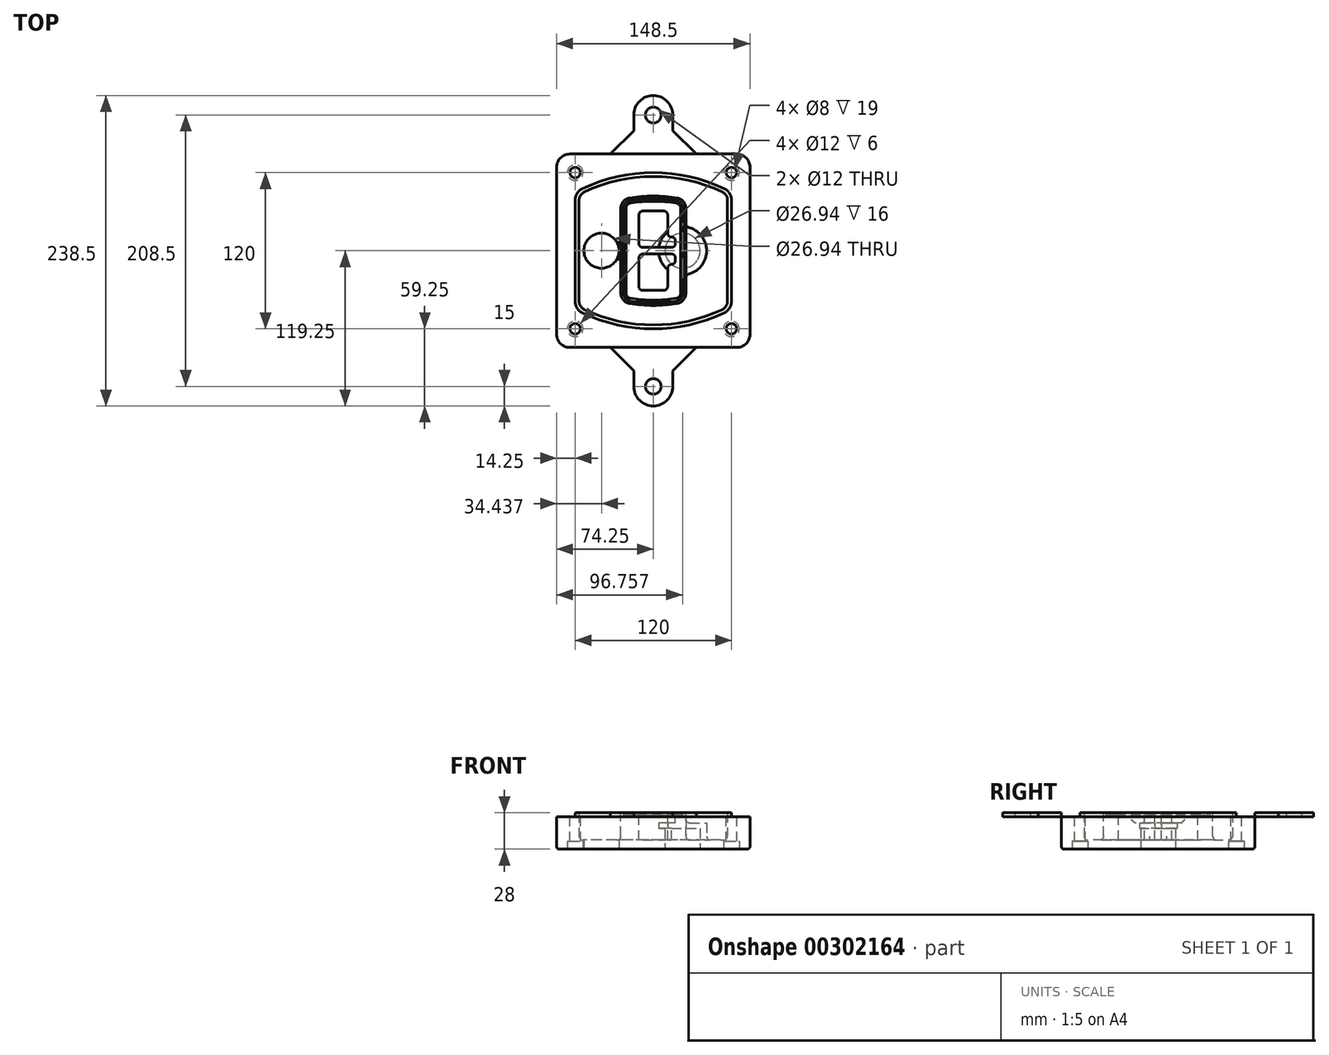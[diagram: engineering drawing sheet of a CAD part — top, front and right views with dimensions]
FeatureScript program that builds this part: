
annotation { "Feature Type Name" : "Feature", "Feature Type Description" : "" }
export const myFeature = defineFeature(function(context is Context, id is Id, definition is map)
    precondition{}
    {
        {
            var Q0;
            Q0=qCreatedBy(makeId("Top.planeOp"),FACE);
            var sketch = newSketch(context, id + "F0", { "sketchPlane" : qUnion([Q0])});
            skPoint(sketch, "E0.rect.middle", {"position": v(0, 0) * mm});
            skLineSegment(sketch, "E1.bottom", {"start": v(-64.25, -74.25) * mm, "end": v(64.25, -74.25) * mm});
            skLineSegment(sketch, "E1.top", {"start": v(-64.25, 74.25) * mm, "end": v(64.25, 74.25) * mm});
            skLineSegment(sketch, "E1.left", {"start": v(-74.25, -64.25) * mm, "end": v(-74.25, 64.25) * mm});
            skLineSegment(sketch, "E1.right", {"start": v(74.25, -64.25) * mm, "end": v(74.25, 64.25) * mm});
            skLineSegment(sketch, "E2", {"start": v(-74.25, 74.25) * mm, "end": v(74.25, -74.25) * mm, "construction": true});
            skLineSegment(sketch, "E3", {"start": v(74.25, 74.25) * mm, "end": v(-74.25, -74.25) * mm, "construction": true});
            skCircle(sketch, "E4", {"center": v(-60, 60) * mm, "radius": 4 * mm});
            skCircle(sketch, "E5", {"center": v(60, 60) * mm, "radius": 4 * mm});
            skCircle(sketch, "E6", {"center": v(60, -60) * mm, "radius": 4 * mm});
            skCircle(sketch, "E7", {"center": v(-60, -60) * mm, "radius": 4 * mm});
            skLineSegment(sketch, "E8", {"start": v(-60, 60) * mm, "end": v(60, 60) * mm, "construction": true});
            skLineSegment(sketch, "E9", {"start": v(60, 60) * mm, "end": v(60, -60) * mm, "construction": true});
            skLineSegment(sketch, "E10", {"start": v(60, -60) * mm, "end": v(-60, -60) * mm, "construction": true});
            skLineSegment(sketch, "E11", {"start": v(-60, -60) * mm, "end": v(-60, 60) * mm, "construction": true});
            skLineSegment(sketch, "E12", {"start": v(-60, 38.83) * mm, "end": v(-60, -38.83) * mm});
            skLineSegment(sketch, "E13", {"start": v(60, 38.83) * mm, "end": v(60, -38.83) * mm});
            skArc(sketch, "E14", {"start": v(54.26, 47.88) * mm, "mid": v(0, 60) * mm, "end": v(-54.26, 47.88) * mm});
            skArc(sketch, "E15", {"start": v(-54.26, -47.88) * mm, "mid": v(0, -60) * mm, "end": v(54.26, -47.88) * mm});
            skLineSegment(sketch, "E16", {"start": v(-60, 0) * mm, "end": v(60, 0) * mm, "construction": true});
            skPoint(sketch, "E17.visualSharp", {"position": v(-60, -45) * mm});
            skArc(sketch, "E17.filletArc", {"start": v(-60, -38.83) * mm, "mid": v(-58.44, -44.2) * mm, "end": v(-54.26, -47.88) * mm});
            skPoint(sketch, "E18.visualSharp", {"position": v(-60, 45) * mm});
            skArc(sketch, "E18.filletArc", {"start": v(-54.26, 47.88) * mm, "mid": v(-58.44, 44.2) * mm, "end": v(-60, 38.83) * mm});
            skPoint(sketch, "E19.visualSharp", {"position": v(60, 45) * mm});
            skArc(sketch, "E19.filletArc", {"start": v(60, 38.83) * mm, "mid": v(58.44, 44.2) * mm, "end": v(54.26, 47.88) * mm});
            skPoint(sketch, "E20.visualSharp", {"position": v(60, -45) * mm});
            skArc(sketch, "E20.filletArc", {"start": v(54.26, -47.88) * mm, "mid": v(58.44, -44.2) * mm, "end": v(60, -38.83) * mm});
            skPoint(sketch, "E21.visualSharp", {"position": v(-74.25, 74.25) * mm});
            skArc(sketch, "E21.filletArc", {"start": v(-64.25, 74.25) * mm, "mid": v(-71.32, 71.32) * mm, "end": v(-74.25, 64.25) * mm});
            skPoint(sketch, "E22.visualSharp", {"position": v(74.25, 74.25) * mm});
            skArc(sketch, "E22.filletArc", {"start": v(74.25, 64.25) * mm, "mid": v(71.32, 71.32) * mm, "end": v(64.25, 74.25) * mm});
            skPoint(sketch, "E23.visualSharp", {"position": v(74.25, -74.25) * mm});
            skArc(sketch, "E23.filletArc", {"start": v(64.25, -74.25) * mm, "mid": v(71.32, -71.32) * mm, "end": v(74.25, -64.25) * mm});
            skPoint(sketch, "E24.visualSharp", {"position": v(-74.25, -74.25) * mm});
            skArc(sketch, "E24.filletArc", {"start": v(-74.25, -64.25) * mm, "mid": v(-71.32, -71.32) * mm, "end": v(-64.25, -74.25) * mm});
            skArc(sketch, "E25.0", {"start": v(57, 38.83) * mm, "mid": v(55.9, 42.58) * mm, "end": v(52.98, 45.17) * mm});
            skLineSegment(sketch, "E25.1", {"start": v(57, 38.83) * mm, "end": v(57, -38.83) * mm});
            skArc(sketch, "E25.2", {"start": v(52.98, -45.17) * mm, "mid": v(55.9, -42.58) * mm, "end": v(57, -38.83) * mm});
            skArc(sketch, "E25.3", {"start": v(-52.98, -45.17) * mm, "mid": v(0, -57) * mm, "end": v(52.98, -45.17) * mm});
            skArc(sketch, "E25.4", {"start": v(-57, -38.83) * mm, "mid": v(-55.9, -42.58) * mm, "end": v(-52.98, -45.17) * mm});
            skArc(sketch, "E25.5", {"start": v(52.98, 45.17) * mm, "mid": v(0, 57) * mm, "end": v(-52.98, 45.17) * mm});
            skLineSegment(sketch, "E25.6", {"start": v(-57, 38.83) * mm, "end": v(-57, -38.83) * mm});
            skArc(sketch, "E25.7", {"start": v(-52.98, 45.17) * mm, "mid": v(-55.9, 42.58) * mm, "end": v(-57, 38.83) * mm});
            skArc(sketch, "E26.0", {"start": v(-55.96, 51.5) * mm, "mid": v(-61.82, 46.33) * mm, "end": v(-64, 38.83) * mm});
            skArc(sketch, "E26.1", {"start": v(55.96, 51.5) * mm, "mid": v(0, 64) * mm, "end": v(-55.96, 51.5) * mm});
            skArc(sketch, "E26.2", {"start": v(64, 38.83) * mm, "mid": v(61.82, 46.33) * mm, "end": v(55.96, 51.5) * mm});
            skLineSegment(sketch, "E26.3", {"start": v(64, 38.83) * mm, "end": v(64, -38.83) * mm});
            skArc(sketch, "E26.4", {"start": v(55.96, -51.5) * mm, "mid": v(61.82, -46.33) * mm, "end": v(64, -38.83) * mm});
            skLineSegment(sketch, "E26.5", {"start": v(-64, 38.83) * mm, "end": v(-64, -38.83) * mm});
            skArc(sketch, "E26.6", {"start": v(-55.96, -51.5) * mm, "mid": v(0, -64) * mm, "end": v(55.96, -51.5) * mm});
            skArc(sketch, "E26.7", {"start": v(-64, -38.83) * mm, "mid": v(-61.82, -46.33) * mm, "end": v(-55.96, -51.5) * mm});
            skSolve(sketch);
        }
        {
            var Q0;
            Q0=makeQuery(id+"F0.imprint","IMPRINT",FACE,{"disambiguationData":[TD([[makeQuery(id+"F0.imprint","IMPRINT",EDGE,{"derivedFrom":sQuery(id+"F0.wireOp",EDGE,"E1.bottom")}),1.0]])]});
            var Q1;
            Q1=makeQuery(id+"F0.imprint","IMPRINT",FACE,{"disambiguationData":[TD([[makeQuery(id+"F0.imprint","IMPRINT",EDGE,{"derivedFrom":sQuery(id+"F0.wireOp",EDGE,"E12")}),1.0]])]});
            var Q2;
            Q2=makeQuery(id+"F0.imprint","IMPRINT",FACE,{"disambiguationData":[TD([[makeQuery(id+"F0.imprint","IMPRINT",EDGE,{"derivedFrom":sQuery(id+"F0.wireOp",EDGE,"E25.0")}),1.0]])]});
            var Q3;
            Q3=makeQuery(id+"F0.imprint","IMPRINT",FACE,{"disambiguationData":[TD([[makeQuery(id+"F0.imprint","IMPRINT",EDGE,{"derivedFrom":sQuery(id+"F0.wireOp",EDGE,"E12")}),-1.0]])]});
            extrude(context, id + "F1", {"entities" : qUnion([Q0, Q1, Q2, Q3]), "oppositeDirection" : true, "depth" : 25 * mm});
        }
        {
            var Q0;
            Q0=makeQuery(id+"F0.imprint","IMPRINT",FACE,{"disambiguationData":[TD([[makeQuery(id+"F0.imprint","IMPRINT",EDGE,{"derivedFrom":sQuery(id+"F0.wireOp",EDGE,"E12")}),1.0]])]});
            extrude(context, id + "F2", {"entities" : qUnion([Q0]), "operationType" : NewBodyOperationType.ADD, "depth" : 3 * mm});
        }
        {
            var Q0;
            Q0=makeQuery(id+"F0.imprint","IMPRINT",FACE,{"disambiguationData":[TD([[makeQuery(id+"F0.imprint","IMPRINT",EDGE,{"derivedFrom":sQuery(id+"F0.wireOp",EDGE,"E25.0")}),1.0]])]});
            extrude(context, id + "F3", {"entities" : qUnion([Q0]), "operationType" : NewBodyOperationType.REMOVE, "oppositeDirection" : true, "depth" : 18 * mm});
        }
        {
            var Q0;
            Q0=makeQuery(id+"F2.opExtrude","CAP_FACE",FACE,{"disambiguationData":[OSD([sQuery(id+"F0.wireOp",EDGE,"E12"),sQuery(id+"F0.wireOp",EDGE,"E13"),sQuery(id+"F0.wireOp",EDGE,"E14"),sQuery(id+"F0.wireOp",EDGE,"E15"),sQuery(id+"F0.wireOp",EDGE,"E17.filletArc"),sQuery(id+"F0.wireOp",EDGE,"E18.filletArc"),sQuery(id+"F0.wireOp",EDGE,"E19.filletArc"),sQuery(id+"F0.wireOp",EDGE,"E20.filletArc"),sQuery(id+"F0.wireOp",EDGE,"E25.0"),sQuery(id+"F0.wireOp",EDGE,"E25.1"),sQuery(id+"F0.wireOp",EDGE,"E25.2"),sQuery(id+"F0.wireOp",EDGE,"E25.3"),sQuery(id+"F0.wireOp",EDGE,"E25.4"),sQuery(id+"F0.wireOp",EDGE,"E25.5"),sQuery(id+"F0.wireOp",EDGE,"E25.6"),sQuery(id+"F0.wireOp",EDGE,"E25.7")])],"isStart":false});
            var sketch = newSketch(context, id + "F4", { "sketchPlane" : qUnion([Q0])});
            skArc(sketch, "E27.0", {"start": v(-18.34, -40.45) * mm, "mid": v(0, -42) * mm, "end": v(18.34, -40.45) * mm});
            skArc(sketch, "E28.0", {"start": v(18.34, 40.45) * mm, "mid": v(0, 42) * mm, "end": v(-18.34, 40.45) * mm});
            skLineSegment(sketch, "E29", {"start": v(-25, 32.57) * mm, "end": v(-25, -32.57) * mm});
            skLineSegment(sketch, "E30", {"start": v(25, 32.57) * mm, "end": v(25, -32.57) * mm});
            skLineSegment(sketch, "E31", {"start": v(-25, 39.1) * mm, "end": v(25, 39.1) * mm, "construction": true});
            skLineSegment(sketch, "E32", {"start": v(-25, -39.1) * mm, "end": v(25, -39.1) * mm, "construction": true});
            skPoint(sketch, "E33.visualSharp", {"position": v(-25, 39.1) * mm});
            skArc(sketch, "E33.filletArc", {"start": v(-18.34, 40.45) * mm, "mid": v(-23.11, 37.73) * mm, "end": v(-25, 32.57) * mm});
            skPoint(sketch, "E34.visualSharp", {"position": v(25, 39.1) * mm});
            skArc(sketch, "E34.filletArc", {"start": v(25, 32.57) * mm, "mid": v(23.11, 37.73) * mm, "end": v(18.34, 40.45) * mm});
            skPoint(sketch, "E35.visualSharp", {"position": v(25, -39.1) * mm});
            skArc(sketch, "E35.filletArc", {"start": v(18.34, -40.45) * mm, "mid": v(23.11, -37.73) * mm, "end": v(25, -32.57) * mm});
            skPoint(sketch, "E36.visualSharp", {"position": v(-25, -39.1) * mm});
            skArc(sketch, "E36.filletArc", {"start": v(-25, -32.57) * mm, "mid": v(-23.11, -37.73) * mm, "end": v(-18.34, -40.45) * mm});
            skArc(sketch, "E37.0", {"start": v(52.98, 45.17) * mm, "mid": v(0, 57) * mm, "end": v(-52.98, 45.17) * mm});
            skArc(sketch, "E37.1", {"start": v(-52.98, 45.17) * mm, "mid": v(-55.9, 42.58) * mm, "end": v(-57, 38.83) * mm});
            skLineSegment(sketch, "E37.2", {"start": v(-57, 38.83) * mm, "end": v(-57, -38.83) * mm});
            skArc(sketch, "E37.3", {"start": v(-57, -38.83) * mm, "mid": v(-55.9, -42.58) * mm, "end": v(-52.98, -45.17) * mm});
            skArc(sketch, "E37.4", {"start": v(-52.98, -45.17) * mm, "mid": v(0, -57) * mm, "end": v(52.98, -45.17) * mm});
            skArc(sketch, "E37.5", {"start": v(52.98, -45.17) * mm, "mid": v(55.9, -42.58) * mm, "end": v(57, -38.83) * mm});
            skLineSegment(sketch, "E37.6", {"start": v(57, 38.83) * mm, "end": v(57, -38.83) * mm});
            skArc(sketch, "E37.7", {"start": v(57, 38.83) * mm, "mid": v(55.9, 42.58) * mm, "end": v(52.98, 45.17) * mm});
            skLineSegment(sketch, "E38.0", {"start": v(23, 32.57) * mm, "end": v(23, -32.57) * mm});
            skArc(sketch, "E38.1", {"start": v(18, -38.48) * mm, "mid": v(21.58, -36.44) * mm, "end": v(23, -32.57) * mm});
            skArc(sketch, "E38.2", {"start": v(-18, -38.48) * mm, "mid": v(0, -40) * mm, "end": v(18, -38.48) * mm});
            skArc(sketch, "E38.3", {"start": v(-23, -32.57) * mm, "mid": v(-21.58, -36.44) * mm, "end": v(-18, -38.48) * mm});
            skLineSegment(sketch, "E38.4", {"start": v(-23, 32.57) * mm, "end": v(-23, -32.57) * mm});
            skArc(sketch, "E38.5", {"start": v(23, 32.57) * mm, "mid": v(21.58, 36.44) * mm, "end": v(18, 38.48) * mm});
            skArc(sketch, "E38.6", {"start": v(-18, 38.48) * mm, "mid": v(-21.58, 36.44) * mm, "end": v(-23, 32.57) * mm});
            skArc(sketch, "E38.7", {"start": v(18, 38.48) * mm, "mid": v(0, 40) * mm, "end": v(-18, 38.48) * mm});
            skArc(sketch, "E39.0", {"start": v(21, 32.57) * mm, "mid": v(20.06, 35.15) * mm, "end": v(17.67, 36.5) * mm});
            skLineSegment(sketch, "E39.1", {"start": v(21, 32.57) * mm, "end": v(21, -32.57) * mm});
            skArc(sketch, "E39.2", {"start": v(17.67, -36.5) * mm, "mid": v(20.06, -35.15) * mm, "end": v(21, -32.57) * mm});
            skArc(sketch, "E39.3", {"start": v(-17.67, -36.5) * mm, "mid": v(0, -38) * mm, "end": v(17.67, -36.5) * mm});
            skArc(sketch, "E39.4", {"start": v(-21, -32.57) * mm, "mid": v(-20.06, -35.15) * mm, "end": v(-17.67, -36.5) * mm});
            skArc(sketch, "E39.5", {"start": v(17.67, 36.5) * mm, "mid": v(0, 38) * mm, "end": v(-17.67, 36.5) * mm});
            skLineSegment(sketch, "E39.6", {"start": v(-21, 32.57) * mm, "end": v(-21, -32.57) * mm});
            skArc(sketch, "E39.7", {"start": v(-17.67, 36.5) * mm, "mid": v(-20.06, 35.15) * mm, "end": v(-21, 32.57) * mm});
            skLineSegment(sketch, "E40", {"start": v(-25, 0) * mm, "end": v(25, 0) * mm, "construction": true});
            skLineSegment(sketch, "E41", {"start": v(-11, 5.5) * mm, "end": v(-11, 27.5) * mm});
            skLineSegment(sketch, "E42", {"start": v(-8, 30.5) * mm, "end": v(8, 30.5) * mm});
            skLineSegment(sketch, "E43", {"start": v(11, 27.5) * mm, "end": v(11, 13.5) * mm});
            skLineSegment(sketch, "E44", {"start": v(14, 10.5) * mm, "end": v(14, 10.5) * mm});
            skLineSegment(sketch, "E45", {"start": v(17, 7.5) * mm, "end": v(17, 5.5) * mm});
            skLineSegment(sketch, "E46", {"start": v(14, 2.5) * mm, "end": v(-8, 2.5) * mm});
            skPoint(sketch, "E47.visualSharp", {"position": v(-11, 30.5) * mm});
            skArc(sketch, "E47.filletArc", {"start": v(-8, 30.5) * mm, "mid": v(-10.12, 29.62) * mm, "end": v(-11, 27.5) * mm});
            skPoint(sketch, "E48.visualSharp", {"position": v(11, 30.5) * mm});
            skArc(sketch, "E48.filletArc", {"start": v(11, 27.5) * mm, "mid": v(10.12, 29.62) * mm, "end": v(8, 30.5) * mm});
            skPoint(sketch, "E49.visualSharp", {"position": v(11, 10.5) * mm});
            skArc(sketch, "E49.filletArc", {"start": v(11, 13.5) * mm, "mid": v(11.88, 11.38) * mm, "end": v(14, 10.5) * mm});
            skPoint(sketch, "E50.visualSharp", {"position": v(17, 10.5) * mm});
            skArc(sketch, "E50.filletArc", {"start": v(17, 7.5) * mm, "mid": v(16.12, 9.62) * mm, "end": v(14, 10.5) * mm});
            skPoint(sketch, "E51.visualSharp", {"position": v(17, 2.5) * mm});
            skArc(sketch, "E51.filletArc", {"start": v(14, 2.5) * mm, "mid": v(16.12, 3.38) * mm, "end": v(17, 5.5) * mm});
            skPoint(sketch, "E52.visualSharp", {"position": v(-11, 2.5) * mm});
            skArc(sketch, "E52.filletArc", {"start": v(-11, 5.5) * mm, "mid": v(-10.12, 3.38) * mm, "end": v(-8, 2.5) * mm});
            skLineSegment(sketch, "E53.0.MirrorCS", {"start": v(14, -2.5) * mm, "end": v(-8, -2.5) * mm});
            skArc(sketch, "E54.0.MirrorCS", {"start": v(-11, -5.5) * mm, "mid": v(-10.12, -3.38) * mm, "end": v(-8, -2.5) * mm});
            skLineSegment(sketch, "E55.0.MirrorCS", {"start": v(-11, -5.5) * mm, "end": v(-11, -27.5) * mm});
            skArc(sketch, "E56.0.MirrorCS", {"start": v(-8, -30.5) * mm, "mid": v(-10.12, -29.62) * mm, "end": v(-11, -27.5) * mm});
            skLineSegment(sketch, "E57.0.MirrorCS", {"start": v(-8, -30.5) * mm, "end": v(8, -30.5) * mm});
            skArc(sketch, "E58.0.MirrorCS", {"start": v(11, -27.5) * mm, "mid": v(10.12, -29.62) * mm, "end": v(8, -30.5) * mm});
            skLineSegment(sketch, "E59.0.MirrorCS", {"start": v(11, -27.5) * mm, "end": v(11, -13.5) * mm});
            skArc(sketch, "E60.0.MirrorCS", {"start": v(11, -13.5) * mm, "mid": v(11.88, -11.38) * mm, "end": v(14, -10.5) * mm});
            skArc(sketch, "E61.0.MirrorCS", {"start": v(17, -7.5) * mm, "mid": v(16.12, -9.62) * mm, "end": v(14, -10.5) * mm});
            skLineSegment(sketch, "E62.0.MirrorCS", {"start": v(17, -7.5) * mm, "end": v(17, -5.5) * mm});
            skArc(sketch, "E63.0.MirrorCS", {"start": v(14, -2.5) * mm, "mid": v(16.12, -3.38) * mm, "end": v(17, -5.5) * mm});
            skSolve(sketch);
        }
        {
            var Q0;
            Q0=makeQuery(id+"F4.imprint","IMPRINT",FACE,{"disambiguationData":[TD([[makeQuery(id+"F4.imprint","IMPRINT",EDGE,{"derivedFrom":sQuery(id+"F4.wireOp",EDGE,"E27.0")}),1.0]])]});
            var Q1;
            Q1=makeQuery(id+"F4.imprint","IMPRINT",FACE,{"disambiguationData":[TD([[makeQuery(id+"F4.imprint","IMPRINT",EDGE,{"derivedFrom":sQuery(id+"F4.wireOp",EDGE,"E38.0")}),-1.0]])]});
            var Q2;
            Q2=makeQuery(id+"F4.imprint","IMPRINT",FACE,{"disambiguationData":[TD([[makeQuery(id+"F4.imprint","IMPRINT",EDGE,{"derivedFrom":sQuery(id+"F4.wireOp",EDGE,"E39.0")}),1.0]])]});
            extrude(context, id + "F5", {"entities" : qUnion([Q0, Q1, Q2]), "operationType" : NewBodyOperationType.ADD, "endBound" : BoundingType.UP_TO_NEXT, "oppositeDirection" : true, "depth" : 25 * mm});
        }
        {
            var Q0;
            Q0=makeQuery(id+"F4.imprint","IMPRINT",FACE,{"disambiguationData":[TD([[makeQuery(id+"F4.imprint","IMPRINT",EDGE,{"derivedFrom":sQuery(id+"F4.wireOp",EDGE,"E38.0")}),-1.0]])]});
            extrude(context, id + "F6", {"entities" : qUnion([Q0]), "operationType" : NewBodyOperationType.REMOVE, "oppositeDirection" : true, "depth" : 2 * mm});
        }
        {
            var Q0;
            Q0=makeQuery(id+"F1.opExtrude","CAP_FACE",FACE,{"disambiguationData":[OSD([sQuery(id+"F0.wireOp",EDGE,"E1.bottom"),sQuery(id+"F0.wireOp",EDGE,"E1.top"),sQuery(id+"F0.wireOp",EDGE,"E1.left"),sQuery(id+"F0.wireOp",EDGE,"E1.right"),sQuery(id+"F0.wireOp",EDGE,"E4"),sQuery(id+"F0.wireOp",EDGE,"E5"),sQuery(id+"F0.wireOp",EDGE,"E6"),sQuery(id+"F0.wireOp",EDGE,"E7"),sQuery(id+"F0.wireOp",EDGE,"E21.filletArc"),sQuery(id+"F0.wireOp",EDGE,"E22.filletArc"),sQuery(id+"F0.wireOp",EDGE,"E23.filletArc"),sQuery(id+"F0.wireOp",EDGE,"E24.filletArc")])],"isStart":false});
            var sketch = newSketch(context, id + "F7", { "sketchPlane" : qUnion([Q0])});
            skCircle(sketch, "E64", {"center": v(22.5, 0) * mm, "radius": 13.47 * mm});
            skCircle(sketch, "E65", {"center": v(-39.81, 0) * mm, "radius": 13.47 * mm});
            skLineSegment(sketch, "E66", {"start": v(74.25, 0) * mm, "end": v(-74.25, 0) * mm});
            skCircle(sketch, "E67", {"center": v(22.5, 0) * mm, "radius": 18.47 * mm});
            skCircle(sketch, "E68", {"center": v(60, -60) * mm, "radius": 6 * mm});
            skCircle(sketch, "E69", {"center": v(-60, -60) * mm, "radius": 6 * mm});
            skCircle(sketch, "E70", {"center": v(-60, 60) * mm, "radius": 6 * mm});
            skCircle(sketch, "E71", {"center": v(60, 60) * mm, "radius": 6 * mm});
            skSolve(sketch);
        }
        {
            var Q0;
            {var subQ1=sQuery(id+"F7.wireOp",EDGE,"E66");var subQ4=sQuery(id+"F7.wireOp",EDGE,"E64");var subQ6=makeQuery(id+"F7.imprint","INTERSECT",VERTEX,{"disambiguationData":[OD(0.0)],"derivedFrom":[subQ4,subQ1]});Q0=makeQuery(id+"F7.imprint","IMPRINT",FACE,{"disambiguationData":[TD([[makeQuery(id+"F7.imprint","IMPRINT",EDGE,{"disambiguationData":[TD([[subQ6,-1.0]])],"derivedFrom":subQ4}),-1.0]])]});}
            var Q1;
            {var subQ0=sQuery(id+"F7.wireOp",EDGE,"E66");var subQ1=sQuery(id+"F7.wireOp",EDGE,"E64");var subQ3=makeQuery(id+"F7.imprint","INTERSECT",VERTEX,{"disambiguationData":[OD(0.0)],"derivedFrom":[subQ1,subQ0]});Q1=makeQuery(id+"F7.imprint","IMPRINT",FACE,{"disambiguationData":[TD([[makeQuery(id+"F7.imprint","IMPRINT",EDGE,{"disambiguationData":[TD([[subQ3,-1.0]])],"derivedFrom":subQ1}),1.0]])]});}
            var Q2;
            {var subQ0=sQuery(id+"F7.wireOp",EDGE,"E66");var subQ1=sQuery(id+"F7.wireOp",EDGE,"E64");var subQ3=makeQuery(id+"F7.imprint","INTERSECT",VERTEX,{"disambiguationData":[OD(0.0)],"derivedFrom":[subQ1,subQ0]});Q2=makeQuery(id+"F7.imprint","IMPRINT",FACE,{"disambiguationData":[TD([[makeQuery(id+"F7.imprint","IMPRINT",EDGE,{"disambiguationData":[TD([[subQ3,1.0]])],"derivedFrom":subQ1}),1.0]])]});}
            var Q3;
            {var subQ1=sQuery(id+"F7.wireOp",EDGE,"E66");var subQ4=sQuery(id+"F7.wireOp",EDGE,"E64");var subQ6=makeQuery(id+"F7.imprint","INTERSECT",VERTEX,{"disambiguationData":[OD(0.0)],"derivedFrom":[subQ4,subQ1]});Q3=makeQuery(id+"F7.imprint","IMPRINT",FACE,{"disambiguationData":[TD([[makeQuery(id+"F7.imprint","IMPRINT",EDGE,{"disambiguationData":[TD([[subQ6,1.0]])],"derivedFrom":subQ4}),-1.0]])]});}
            extrude(context, id + "F8", {"entities" : qUnion([Q0, Q1, Q2, Q3]), "operationType" : NewBodyOperationType.ADD, "oppositeDirection" : true, "depth" : 20 * mm});
        }
        {
            var Q0;
            {var subQ0=sQuery(id+"F7.wireOp",EDGE,"E66");var subQ1=sQuery(id+"F7.wireOp",EDGE,"E64");var subQ3=makeQuery(id+"F7.imprint","INTERSECT",VERTEX,{"disambiguationData":[OD(0.0)],"derivedFrom":[subQ1,subQ0]});Q0=makeQuery(id+"F7.imprint","IMPRINT",FACE,{"disambiguationData":[TD([[makeQuery(id+"F7.imprint","IMPRINT",EDGE,{"disambiguationData":[TD([[subQ3,-1.0]])],"derivedFrom":subQ1}),1.0]])]});}
            var Q1;
            {var subQ0=sQuery(id+"F7.wireOp",EDGE,"E66");var subQ1=sQuery(id+"F7.wireOp",EDGE,"E64");var subQ3=makeQuery(id+"F7.imprint","INTERSECT",VERTEX,{"disambiguationData":[OD(0.0)],"derivedFrom":[subQ1,subQ0]});Q1=makeQuery(id+"F7.imprint","IMPRINT",FACE,{"disambiguationData":[TD([[makeQuery(id+"F7.imprint","IMPRINT",EDGE,{"disambiguationData":[TD([[subQ3,1.0]])],"derivedFrom":subQ1}),1.0]])]});}
            extrude(context, id + "F9", {"entities" : qUnion([Q0, Q1]), "operationType" : NewBodyOperationType.REMOVE, "oppositeDirection" : true, "depth" : 16 * mm});
        }
        {
            var Q0;
            {var subQ0=sQuery(id+"F7.wireOp",EDGE,"E66");var subQ1=sQuery(id+"F7.wireOp",EDGE,"E65");var subQ3=makeQuery(id+"F7.imprint","INTERSECT",VERTEX,{"disambiguationData":[OD(0.0)],"derivedFrom":[subQ1,subQ0]});Q0=makeQuery(id+"F7.imprint","IMPRINT",FACE,{"disambiguationData":[TD([[makeQuery(id+"F7.imprint","IMPRINT",EDGE,{"disambiguationData":[TD([[subQ3,-1.0]])],"derivedFrom":subQ1}),1.0]])]});}
            var Q1;
            {var subQ0=sQuery(id+"F7.wireOp",EDGE,"E66");var subQ1=sQuery(id+"F7.wireOp",EDGE,"E65");var subQ3=makeQuery(id+"F7.imprint","INTERSECT",VERTEX,{"disambiguationData":[OD(0.0)],"derivedFrom":[subQ1,subQ0]});Q1=makeQuery(id+"F7.imprint","IMPRINT",FACE,{"disambiguationData":[TD([[makeQuery(id+"F7.imprint","IMPRINT",EDGE,{"disambiguationData":[TD([[subQ3,1.0]])],"derivedFrom":subQ1}),1.0]])]});}
            extrude(context, id + "F10", {"entities" : qUnion([Q0, Q1]), "operationType" : NewBodyOperationType.REMOVE, "oppositeDirection" : true, "depth" : 25 * mm});
        }
        {
            var Q0;
            Q0=makeQuery(id+"F7.imprint","IMPRINT",FACE,{"disambiguationData":[TD([[makeQuery(id+"F7.imprint","IMPRINT",EDGE,{"derivedFrom":sQuery(id+"F7.wireOp",EDGE,"E68")}),1.0]])]});
            var Q1;
            Q1=makeQuery(id+"F7.imprint","IMPRINT",FACE,{"disambiguationData":[TD([[makeQuery(id+"F7.imprint","IMPRINT",EDGE,{"derivedFrom":makeQuery(id+"F1.opExtrude","CAP_EDGE",EDGE,{"disambiguationData":[OSD([sQuery(id+"F0.wireOp",EDGE,"E5")])],"isStart":false})}),-1.0]])]});
            var Q2;
            Q2=makeQuery(id+"F7.imprint","IMPRINT",FACE,{"disambiguationData":[TD([[makeQuery(id+"F7.imprint","IMPRINT",EDGE,{"derivedFrom":sQuery(id+"F7.wireOp",EDGE,"E69")}),1.0]])]});
            var Q3;
            Q3=makeQuery(id+"F7.imprint","IMPRINT",FACE,{"disambiguationData":[TD([[makeQuery(id+"F7.imprint","IMPRINT",EDGE,{"derivedFrom":makeQuery(id+"F1.opExtrude","CAP_EDGE",EDGE,{"disambiguationData":[OSD([sQuery(id+"F0.wireOp",EDGE,"E4")])],"isStart":false})}),-1.0]])]});
            var Q4;
            Q4=makeQuery(id+"F7.imprint","IMPRINT",FACE,{"disambiguationData":[TD([[makeQuery(id+"F7.imprint","IMPRINT",EDGE,{"derivedFrom":sQuery(id+"F7.wireOp",EDGE,"E70")}),1.0]])]});
            var Q5;
            Q5=makeQuery(id+"F7.imprint","IMPRINT",FACE,{"disambiguationData":[TD([[makeQuery(id+"F7.imprint","IMPRINT",EDGE,{"derivedFrom":makeQuery(id+"F1.opExtrude","CAP_EDGE",EDGE,{"disambiguationData":[OSD([sQuery(id+"F0.wireOp",EDGE,"E7")])],"isStart":false})}),-1.0]])]});
            var Q6;
            Q6=makeQuery(id+"F7.imprint","IMPRINT",FACE,{"disambiguationData":[TD([[makeQuery(id+"F7.imprint","IMPRINT",EDGE,{"derivedFrom":sQuery(id+"F7.wireOp",EDGE,"E71")}),1.0]])]});
            var Q7;
            Q7=makeQuery(id+"F7.imprint","IMPRINT",FACE,{"disambiguationData":[TD([[makeQuery(id+"F7.imprint","IMPRINT",EDGE,{"derivedFrom":makeQuery(id+"F1.opExtrude","CAP_EDGE",EDGE,{"disambiguationData":[OSD([sQuery(id+"F0.wireOp",EDGE,"E6")])],"isStart":false})}),-1.0]])]});
            extrude(context, id + "F11", {"entities" : qUnion([Q0, Q1, Q2, Q3, Q4, Q5, Q6, Q7]), "operationType" : NewBodyOperationType.REMOVE, "oppositeDirection" : true, "depth" : 6 * mm});
        }
        {
            var Q0;
            Q0=makeQuery(id+"F9.boolean.opBoolean","COPY",FACE,{"derivedFrom":makeQuery(id+"F9.opExtrude","CAP_FACE",FACE,{"disambiguationData":[OSD([sQuery(id+"F7.wireOp",EDGE,"E64")])],"isStart":false})});
            var sketch = newSketch(context, id + "F12", { "sketchPlane" : qUnion([Q0])});
            skArc(sketch, "E72.0", {"start": v(11, 14.45) * mm, "mid": v(6.45, 9.13) * mm, "end": v(4.2, 2.5) * mm});
            skArc(sketch, "E72.1", {"start": v(4.2, -2.5) * mm, "mid": v(6.45, -9.13) * mm, "end": v(11, -14.45) * mm});
            skLineSegment(sketch, "E73", {"start": v(4.2, -2.5) * mm, "end": v(14, -2.5) * mm});
            skLineSegment(sketch, "E74.0", {"start": v(14, 2.5) * mm, "end": v(4.2, 2.5) * mm});
            skArc(sketch, "E74.1", {"start": v(14, 2.5) * mm, "mid": v(16.12, 3.38) * mm, "end": v(17, 5.5) * mm});
            skLineSegment(sketch, "E74.2", {"start": v(17, 7.5) * mm, "end": v(17, 5.5) * mm});
            skArc(sketch, "E74.3", {"start": v(17, 7.5) * mm, "mid": v(16.12, 9.62) * mm, "end": v(14, 10.5) * mm});
            skArc(sketch, "E74.4", {"start": v(11, 13.5) * mm, "mid": v(11.88, 11.38) * mm, "end": v(14, 10.5) * mm});
            skLineSegment(sketch, "E74.5", {"start": v(11, 14.45) * mm, "end": v(11, 13.5) * mm});
            skLineSegment(sketch, "E74.7", {"start": v(14, -2.5) * mm, "end": v(4.2, -2.5) * mm});
            skArc(sketch, "E74.8", {"start": v(14, -2.5) * mm, "mid": v(16.12, -3.38) * mm, "end": v(17, -5.5) * mm});
            skLineSegment(sketch, "E74.9", {"start": v(17, -7.5) * mm, "end": v(17, -5.5) * mm});
            skArc(sketch, "E74.10", {"start": v(17, -7.5) * mm, "mid": v(16.12, -9.62) * mm, "end": v(14, -10.5) * mm});
            skArc(sketch, "E74.11", {"start": v(11, -13.5) * mm, "mid": v(11.88, -11.38) * mm, "end": v(14, -10.5) * mm});
            skLineSegment(sketch, "E74.12", {"start": v(11, -14.45) * mm, "end": v(11, -13.5) * mm});
            skPoint(sketch, "E75.orphan", {"position": v(11, -27.5) * mm});
            skPoint(sketch, "E76.orphan", {"position": v(-8, -2.5) * mm});
            skPoint(sketch, "E77.orphan", {"position": v(-8, 2.5) * mm});
            skPoint(sketch, "E78.orphan", {"position": v(11, 27.5) * mm});
            skSolve(sketch);
        }
        {
            var Q0;
            {var subQ7=sQuery(id+"F12.wireOp",EDGE,"E72.0");var subQ14=sQuery(id+"F12.wireOp",EDGE,"E72.1");var subQ16=sQuery(id+"F12.wireOp",EDGE,"E74.1");var subQ18=sQuery(id+"F12.wireOp",EDGE,"E74.8");Q0=qUnion([makeQuery(id+"F12.imprint","IMPRINT",FACE,{"disambiguationData":[TD([[makeQuery(id+"F12.imprint","IMPRINT",EDGE,{"derivedFrom":subQ7}),1.0]])]}),makeQuery(id+"F12.imprint","IMPRINT",FACE,{"disambiguationData":[TD([[makeQuery(id+"F12.imprint","IMPRINT",EDGE,{"derivedFrom":subQ14}),1.0]])]}),makeQuery(id+"F12.imprint","IMPRINT",FACE,{"disambiguationData":[TD([[makeQuery(id+"F12.imprint","IMPRINT",EDGE,{"derivedFrom":subQ16}),1.0]])]}),makeQuery(id+"F12.imprint","IMPRINT",FACE,{"disambiguationData":[TD([[makeQuery(id+"F12.imprint","IMPRINT",EDGE,{"derivedFrom":subQ18}),-1.0]])]})]);}
            var Q1;
            Q1=makeQuery(id+"F5.boolean.opBoolean","SPLIT",FACE,{"disambiguationData":[TD([makeQuery(id+"F5.opExtrude","SWEPT_FACE",FACE,{"disambiguationData":[OSD([sQuery(id+"F4.wireOp",EDGE,"E41")])]})])],"derivedFrom":makeQuery(id+"F3.boolean.opBoolean","COPY",FACE,{"derivedFrom":makeQuery(id+"F3.opExtrude","CAP_FACE",FACE,{"disambiguationData":[OSD([sQuery(id+"F0.wireOp",EDGE,"E25.0"),sQuery(id+"F0.wireOp",EDGE,"E25.1"),sQuery(id+"F0.wireOp",EDGE,"E25.2"),sQuery(id+"F0.wireOp",EDGE,"E25.3"),sQuery(id+"F0.wireOp",EDGE,"E25.4"),sQuery(id+"F0.wireOp",EDGE,"E25.5"),sQuery(id+"F0.wireOp",EDGE,"E25.6"),sQuery(id+"F0.wireOp",EDGE,"E25.7")])],"isStart":false})})});
            extrude(context, id + "F13", {"entities" : qUnion([Q0]), "operationType" : NewBodyOperationType.REMOVE, "endBound" : BoundingType.UP_TO_SURFACE, "endBoundEntityFace" : qUnion([Q1]), "depth" : 25 * mm});
        }
        {
            var Q0;
            Q0=makeQuery(id+"F3.boolean.opBoolean","COPY",EDGE,{"derivedFrom":makeQuery(id+"F3.opExtrude","CAP_EDGE",EDGE,{"disambiguationData":[OSD([sQuery(id+"F0.wireOp",EDGE,"E25.6")])],"isStart":false})});
            var Q1;
            Q1=makeQuery(id+"F8.boolean.opBoolean","INTERSECT",EDGE,{"derivedFrom":[makeQuery(id+"F5.opExtrude","SWEPT_FACE",FACE,{"disambiguationData":[OSD([sQuery(id+"F4.wireOp",EDGE,"E30")])]}),makeQuery(id+"F8.opExtrude","CAP_FACE",FACE,{"disambiguationData":[OSD([sQuery(id+"F7.wireOp",EDGE,"E67")])],"isStart":false})]});
            var Q2;
            Q2=makeQuery(id+"F8.boolean.opBoolean","INTERSECT",EDGE,{"disambiguationData":[OD(1.0)],"derivedFrom":[makeQuery(id+"F5.opExtrude","SWEPT_FACE",FACE,{"disambiguationData":[OSD([sQuery(id+"F4.wireOp",EDGE,"E30")])]}),makeQuery(id+"F8.opExtrude","SWEPT_FACE",FACE,{"disambiguationData":[OSD([sQuery(id+"F7.wireOp",EDGE,"E67")])]})]});
            var Q3;
            {var subQ0=sQuery(id+"F4.wireOp",EDGE,"E30");Q3=makeQuery(id+"F8.boolean.opBoolean","SPLIT",EDGE,{"disambiguationData":[TD([makeQuery(id+"F5.opExtrude","SWEPT_FACE",FACE,{"disambiguationData":[OSD([sQuery(id+"F4.wireOp",EDGE,"E35.filletArc")])]})])],"derivedFrom":makeQuery(id+"F5.opExtrude","CAP_EDGE",EDGE,{"disambiguationData":[OSD([subQ0])],"isStart":false})});}
            var Q4;
            {var subQ0=sQuery(id+"F0.wireOp",EDGE,"E25.7");var subQ1=sQuery(id+"F0.wireOp",EDGE,"E25.1");var subQ2=sQuery(id+"F0.wireOp",EDGE,"E25.6");var subQ3=sQuery(id+"F0.wireOp",EDGE,"E25.5");var subQ4=sQuery(id+"F0.wireOp",EDGE,"E25.4");var subQ5=sQuery(id+"F0.wireOp",EDGE,"E25.0");var subQ6=sQuery(id+"F0.wireOp",EDGE,"E25.2");var subQ7=sQuery(id+"F0.wireOp",EDGE,"E25.3");Q4=makeQuery(id+"F8.boolean.opBoolean","INTERSECT",EDGE,{"derivedFrom":[makeQuery(id+"F5.boolean.opBoolean","SPLIT",FACE,{"disambiguationData":[TD([makeQuery(id+"F2.opExtrude","SWEPT_FACE",FACE,{"disambiguationData":[OSD([subQ5])]})])],"derivedFrom":makeQuery(id+"F3.boolean.opBoolean","COPY",FACE,{"derivedFrom":makeQuery(id+"F3.opExtrude","CAP_FACE",FACE,{"disambiguationData":[OSD([subQ5,subQ1,subQ6,subQ7,subQ4,subQ3,subQ2,subQ0])],"isStart":false})})}),makeQuery(id+"F8.opExtrude","SWEPT_FACE",FACE,{"disambiguationData":[OSD([sQuery(id+"F7.wireOp",EDGE,"E67")])]})]});}
            var Q5;
            Q5=makeQuery(id+"F8.boolean.opBoolean","INTERSECT",EDGE,{"disambiguationData":[OD(0.0)],"derivedFrom":[makeQuery(id+"F5.opExtrude","SWEPT_FACE",FACE,{"disambiguationData":[OSD([sQuery(id+"F4.wireOp",EDGE,"E30")])]}),makeQuery(id+"F8.opExtrude","SWEPT_FACE",FACE,{"disambiguationData":[OSD([sQuery(id+"F7.wireOp",EDGE,"E67")])]})]});
            fillet(context, id + "F14", {"entities" : qUnion([Q0, Q1, Q2, Q3, Q4, Q5]), "radius" : 3 * mm, "tangentPropagation" : true, "allowEdgeOverflow" : false});
        }
        {
            var Q0;
            Q0=makeQuery(id+"F1.opExtrude","CAP_EDGE",EDGE,{"disambiguationData":[OSD([sQuery(id+"F0.wireOp",EDGE,"E1.bottom")])],"isStart":false});
            fillet(context, id + "F15", {"entities" : qUnion([Q0]), "radius" : 2 * mm, "tangentPropagation" : true, "allowEdgeOverflow" : false});
        }
        {
            var Q0;
            {var subQ0=sQuery(id+"F0.wireOp",EDGE,"E21.filletArc");var subQ1=sQuery(id+"F0.wireOp",EDGE,"E7");var subQ2=sQuery(id+"F0.wireOp",EDGE,"E6");var subQ3=sQuery(id+"F0.wireOp",EDGE,"E5");var subQ4=sQuery(id+"F0.wireOp",EDGE,"E4");var subQ5=sQuery(id+"F0.wireOp",EDGE,"E22.filletArc");var subQ6=sQuery(id+"F0.wireOp",EDGE,"E1.bottom");var subQ7=sQuery(id+"F0.wireOp",EDGE,"E1.right");var subQ8=sQuery(id+"F0.wireOp",EDGE,"E1.top");var subQ9=sQuery(id+"F0.wireOp",EDGE,"E1.left");var subQ10=sQuery(id+"F0.wireOp",EDGE,"E23.filletArc");var subQ11=sQuery(id+"F0.wireOp",EDGE,"E24.filletArc");Q0=makeQuery(id+"F2.boolean.opBoolean","SPLIT",FACE,{"disambiguationData":[TD([makeQuery(id+"F1.opExtrude","SWEPT_FACE",FACE,{"disambiguationData":[OSD([subQ6])]})])],"derivedFrom":makeQuery(id+"F1.opExtrude","CAP_FACE",FACE,{"disambiguationData":[OSD([subQ6,subQ8,subQ9,subQ7,subQ4,subQ3,subQ2,subQ1,subQ0,subQ5,subQ10,subQ11])],"isStart":true})});}
            var sketch = newSketch(context, id + "F16", { "sketchPlane" : qUnion([Q0])});
            skCircle(sketch, "E79", {"center": v(0, 104.25) * mm, "radius": 6 * mm});
            skArc(sketch, "E80", {"start": v(15, 104.25) * mm, "mid": v(0, 119.25) * mm, "end": v(-15, 104.25) * mm});
            skLineSegment(sketch, "E81", {"start": v(-15, 104.25) * mm, "end": v(-15, 92.25) * mm});
            skLineSegment(sketch, "E82", {"start": v(-15, 92.25) * mm, "end": v(-33, 74.25) * mm});
            skLineSegment(sketch, "E83", {"start": v(15, 104.25) * mm, "end": v(15, 92.25) * mm});
            skLineSegment(sketch, "E84", {"start": v(15, 92.25) * mm, "end": v(33, 74.25) * mm});
            skLineSegment(sketch, "E85", {"start": v(0, 74.25) * mm, "end": v(0, 104.25) * mm, "construction": true});
            skLineSegment(sketch, "E86", {"start": v(0, 0) * mm, "end": v(-128.38, 0) * mm, "construction": true});
            skPoint(sketch, "E86.endSnap0", {"position": v(-74.25, 0) * mm});
            skLineSegment(sketch, "E87", {"start": v(-128.38, 0) * mm, "end": v(137.8, 0) * mm, "construction": true});
            skLineSegment(sketch, "E88.MirrorCS", {"start": v(-15, -104.25) * mm, "end": v(-15, -92.25) * mm});
            skLineSegment(sketch, "E89.MirrorCS", {"start": v(15, -104.25) * mm, "end": v(15, -92.25) * mm});
            skLineSegment(sketch, "E90.MirrorCS", {"start": v(-15, -92.25) * mm, "end": v(-33, -74.25) * mm});
            skLineSegment(sketch, "E91.MirrorCS", {"start": v(15, -92.25) * mm, "end": v(33, -74.25) * mm});
            skCircle(sketch, "E92.MirrorC", {"center": v(0, -104.25) * mm, "radius": 6 * mm});
            skLineSegment(sketch, "E93.MirrorCS", {"start": v(0, -74.25) * mm, "end": v(0, -104.25) * mm, "construction": true});
            skArc(sketch, "E94.MirrorCS", {"start": v(15, -104.25) * mm, "mid": v(0, -119.25) * mm, "end": v(-15, -104.25) * mm});
            skSolve(sketch);
        }
        {
            var Q0;
            Q0=makeQuery(id+"F16.imprint","IMPRINT",FACE,{"disambiguationData":[TD([[makeQuery(id+"F16.imprint","IMPRINT",EDGE,{"derivedFrom":sQuery(id+"F16.wireOp",EDGE,"E79")}),-1.0]])]});
            var Q1;
            Q1=makeQuery(id+"F16.imprint","IMPRINT",FACE,{"disambiguationData":[TD([[makeQuery(id+"F16.imprint","IMPRINT",EDGE,{"derivedFrom":sQuery(id+"F16.wireOp",EDGE,"E88.MirrorCS")}),-1.0]])]});
            var Q2;
            Q2=makeQuery(id+"F16.imprint","IMPRINT",FACE,{"disambiguationData":[TD([[makeQuery(id+"F16.imprint","IMPRINT",EDGE,{"derivedFrom":makeQuery(id+"F2.opExtrude","CAP_EDGE",EDGE,{"disambiguationData":[OSD([sQuery(id+"F0.wireOp",EDGE,"E12")])],"isStart":true})}),1.0]])]});
            var Q3;
            Q3=makeQuery(id+"F2.opExtrude","CAP_FACE",FACE,{"disambiguationData":[OSD([sQuery(id+"F0.wireOp",EDGE,"E12"),sQuery(id+"F0.wireOp",EDGE,"E13"),sQuery(id+"F0.wireOp",EDGE,"E14"),sQuery(id+"F0.wireOp",EDGE,"E15"),sQuery(id+"F0.wireOp",EDGE,"E17.filletArc"),sQuery(id+"F0.wireOp",EDGE,"E18.filletArc"),sQuery(id+"F0.wireOp",EDGE,"E19.filletArc"),sQuery(id+"F0.wireOp",EDGE,"E20.filletArc"),sQuery(id+"F0.wireOp",EDGE,"E25.0"),sQuery(id+"F0.wireOp",EDGE,"E25.1"),sQuery(id+"F0.wireOp",EDGE,"E25.2"),sQuery(id+"F0.wireOp",EDGE,"E25.3"),sQuery(id+"F0.wireOp",EDGE,"E25.4"),sQuery(id+"F0.wireOp",EDGE,"E25.5"),sQuery(id+"F0.wireOp",EDGE,"E25.6"),sQuery(id+"F0.wireOp",EDGE,"E25.7")])],"isStart":false});
            extrude(context, id + "F17", {"entities" : qUnion([Q0, Q1, Q2]), "endBound" : BoundingType.UP_TO_SURFACE, "endBoundEntityFace" : qUnion([Q3]), "depth" : 25 * mm});
        }
    });
